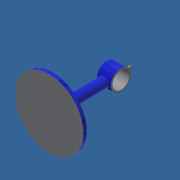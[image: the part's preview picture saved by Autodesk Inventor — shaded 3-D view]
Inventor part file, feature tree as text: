
AUTODESK INVENTOR PART (.ipt)
format: ipt  version: 2018 (Build 220112000, 112)  size: 125,952 bytes
history: native  units: mm
features: extrude x4, sketch x4, fillet x1
ambient origin geometry x8: Origin, YZ Plane, XZ Plane, XY Plane, X Axis, Y Axis, Z Axis, Center Point
bodies: Solid1 (feature_tree)
feature tree (9):
  extrude  "Extrusion1"  Depth=10.0mm TaperAngle=0.0deg
  extrude  "Extrusion2"  Depth=30.0mm
  fillet  "Fillet1"  Radius=20.0mm
  extrude  "Extrusion3"  Depth=60.0mm
  extrude  "Extrusion4"  Depth=5.0mm
  sketch  "Sketch1"  dims[d0=200.0mm d1=10.0mm d2=0.0mm]
  sketch  "Sketch2"  dims[d3=150.0mm d4=0.0mm d5=30.0mm d6=20.0mm]
  sketch  "Sketch3"  dims[d7=50.0mm d8=60.0mm]
  sketch  "Sketch4"  dims[d9=40.0mm d10=0.0mm d11=3.0mm d12=5.0mm d13=0.0mm]
